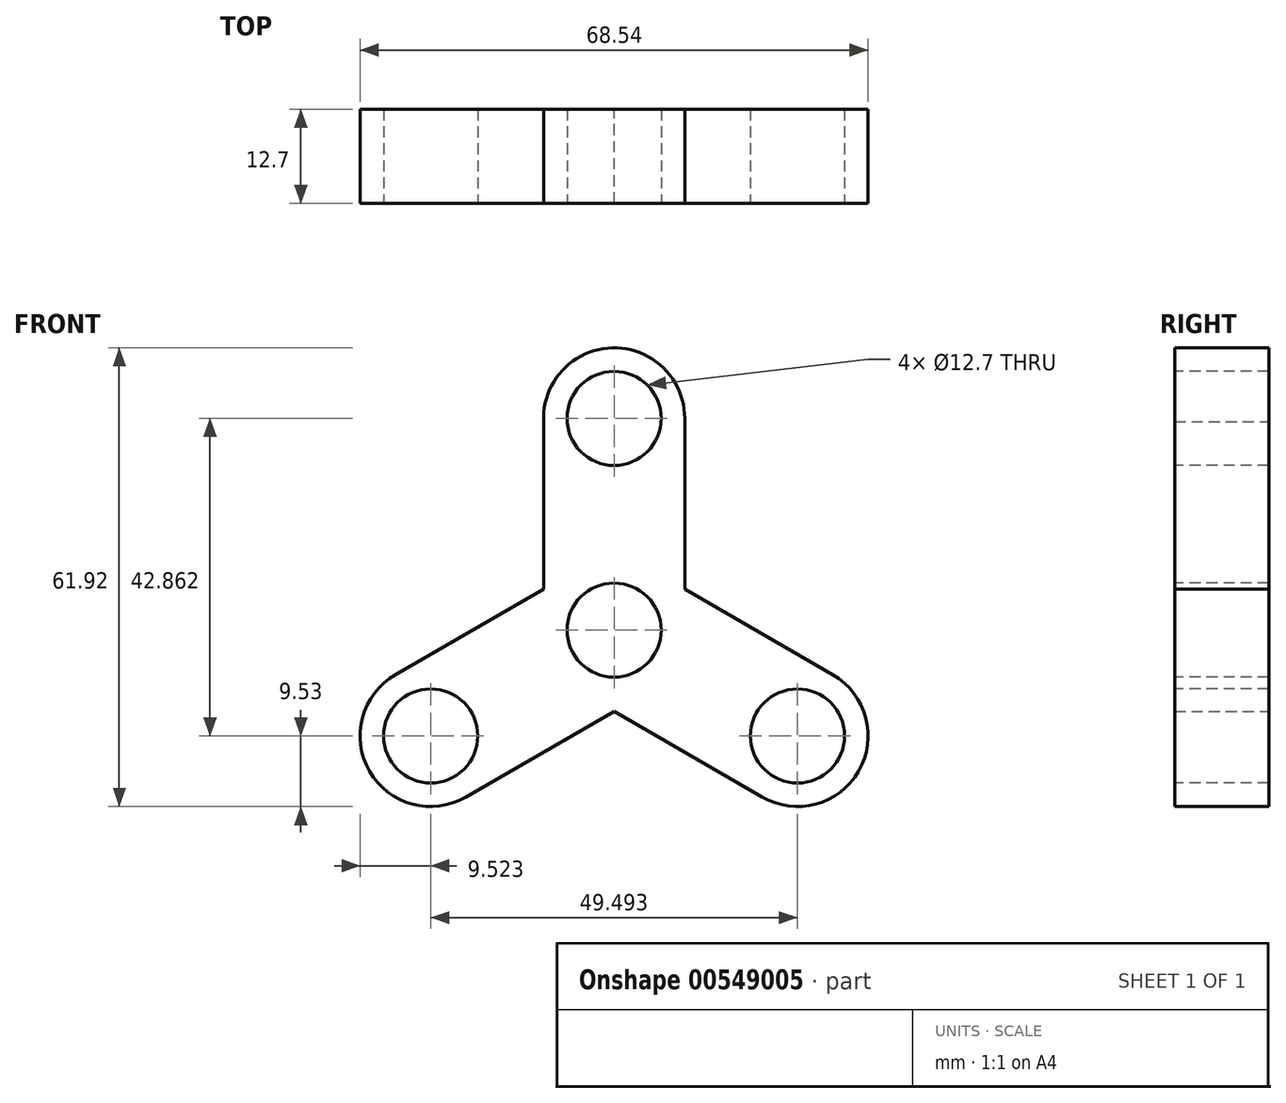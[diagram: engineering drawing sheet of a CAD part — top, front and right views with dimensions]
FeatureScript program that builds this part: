
annotation { "Feature Type Name" : "Feature", "Feature Type Description" : "" }
export const myFeature = defineFeature(function(context is Context, id is Id, definition is map)
    precondition{}
    {
        {
            var Q0;
            Q0=qCreatedBy(makeId("Front.planeOp"),FACE);
            var sketch = newSketch(context, id + "F0", { "sketchPlane" : qUnion([Q0])});
            skCircle(sketch, "E0", {"center": v(0, 42.86) * mm, "radius": 9.53 * mm});
            skCircle(sketch, "E1", {"center": v(-24.75, 0) * mm, "radius": 9.53 * mm});
            skCircle(sketch, "E2", {"center": v(24.75, 0) * mm, "radius": 9.53 * mm});
            skLineSegment(sketch, "E3", {"start": v(-29.5, 8.25) * mm, "end": v(-4.76, 22.54) * mm});
            skLineSegment(sketch, "E4", {"start": v(-19.98, -8.25) * mm, "end": v(4.76, 6.04) * mm});
            skLineSegment(sketch, "E5", {"start": v(9.52, 42.86) * mm, "end": v(9.53, 14.29) * mm});
            skLineSegment(sketch, "E6", {"start": v(-9.51, 42.4) * mm, "end": v(-9.51, 13.83) * mm});
            skLineSegment(sketch, "E7", {"start": v(29.5, 8.25) * mm, "end": v(4.76, 22.54) * mm});
            skLineSegment(sketch, "E8", {"start": v(19.98, -8.25) * mm, "end": v(-4.76, 6.04) * mm});
            skSolve(sketch);
        }
        {
            var Q0;
            {var subQ0=sQuery(id+"F0.wireOp",EDGE,"E0");var subQ1=makeQuery(id+"F0.imprint","INTERSECT",VERTEX,{"derivedFrom":[subQ0,sQuery(id+"F0.wireOp",EDGE,"E5")]});Q0=makeQuery(id+"F0.imprint","IMPRINT",FACE,{"disambiguationData":[TD([[makeQuery(id+"F0.imprint","IMPRINT",EDGE,{"disambiguationData":[TD([[subQ1,-1.0]])],"derivedFrom":subQ0}),1.0]])]});}
            var Q1;
            {var subQ12=sQuery(id+"F0.wireOp",EDGE,"E5");var subQ13=sQuery(id+"F0.wireOp",EDGE,"E0");var subQ14=makeQuery(id+"F0.imprint","INTERSECT",VERTEX,{"derivedFrom":[subQ13,subQ12]});Q1=makeQuery(id+"F0.imprint","IMPRINT",FACE,{"disambiguationData":[TD([[makeQuery(id+"F0.imprint","IMPRINT",EDGE,{"disambiguationData":[TD([[subQ14,1.0]])],"derivedFrom":subQ13}),-1.0]])]});}
            var Q2;
            {var subQ0=sQuery(id+"F0.wireOp",EDGE,"E1");var subQ1=makeQuery(id+"F0.imprint","INTERSECT",VERTEX,{"derivedFrom":[subQ0,sQuery(id+"F0.wireOp",EDGE,"E3")]});Q2=makeQuery(id+"F0.imprint","IMPRINT",FACE,{"disambiguationData":[TD([[makeQuery(id+"F0.imprint","IMPRINT",EDGE,{"disambiguationData":[TD([[subQ1,-1.0]])],"derivedFrom":subQ0}),1.0]])]});}
            var Q3;
            {var subQ0=sQuery(id+"F0.wireOp",EDGE,"E2");var subQ1=makeQuery(id+"F0.imprint","INTERSECT",VERTEX,{"derivedFrom":[subQ0,sQuery(id+"F0.wireOp",EDGE,"E7")]});Q3=makeQuery(id+"F0.imprint","IMPRINT",FACE,{"disambiguationData":[TD([[makeQuery(id+"F0.imprint","IMPRINT",EDGE,{"disambiguationData":[TD([[subQ1,-1.0]])],"derivedFrom":subQ0}),1.0]])]});}
            extrude(context, id + "F1", {"entities" : qUnion([Q0, Q1, Q2, Q3]), "depth" : 12.7 * mm, "offsetDistance" : 25.4 * mm});
        }
        {
            var Q0;
            Q0=makeQuery(id+"F1.opExtrude","CAP_FACE",FACE,{"disambiguationData":[OSD([sQuery(id+"F0.wireOp",EDGE,"E0"),sQuery(id+"F0.wireOp",EDGE,"E1"),sQuery(id+"F0.wireOp",EDGE,"E2"),sQuery(id+"F0.wireOp",EDGE,"E3"),sQuery(id+"F0.wireOp",EDGE,"E4"),sQuery(id+"F0.wireOp",EDGE,"E5"),sQuery(id+"F0.wireOp",EDGE,"E6"),sQuery(id+"F0.wireOp",EDGE,"E7"),sQuery(id+"F0.wireOp",EDGE,"E8")])],"isStart":false});
            var sketch = newSketch(context, id + "F2", { "sketchPlane" : qUnion([Q0])});
            skCircle(sketch, "E9", {"center": v(-24.75, 0) * mm, "radius": 6.35 * mm});
            skCircle(sketch, "E10", {"center": v(24.75, 0) * mm, "radius": 6.35 * mm});
            skCircle(sketch, "E11", {"center": v(0, 42.86) * mm, "radius": 6.35 * mm});
            skCircle(sketch, "E12", {"center": v(0, 14.29) * mm, "radius": 6.35 * mm});
            skSolve(sketch);
        }
        {
            var Q0;
            Q0=makeQuery(id+"F2.imprint","IMPRINT",FACE,{"disambiguationData":[TD([[makeQuery(id+"F2.imprint","IMPRINT",EDGE,{"derivedFrom":sQuery(id+"F2.wireOp",EDGE,"E9")}),1.0]])]});
            var Q1;
            Q1=makeQuery(id+"F2.imprint","IMPRINT",FACE,{"disambiguationData":[TD([[makeQuery(id+"F2.imprint","IMPRINT",EDGE,{"derivedFrom":sQuery(id+"F2.wireOp",EDGE,"E12")}),1.0]])]});
            var Q2;
            Q2=makeQuery(id+"F2.imprint","IMPRINT",FACE,{"disambiguationData":[TD([[makeQuery(id+"F2.imprint","IMPRINT",EDGE,{"derivedFrom":sQuery(id+"F2.wireOp",EDGE,"E11")}),1.0]])]});
            var Q3;
            Q3=makeQuery(id+"F2.imprint","IMPRINT",FACE,{"disambiguationData":[TD([[makeQuery(id+"F2.imprint","IMPRINT",EDGE,{"derivedFrom":sQuery(id+"F2.wireOp",EDGE,"E10")}),1.0]])]});
            extrude(context, id + "F3", {"entities" : qUnion([Q0, Q1, Q2, Q3]), "operationType" : NewBodyOperationType.REMOVE, "endBound" : BoundingType.THROUGH_ALL, "oppositeDirection" : true, "depth" : 25.4 * mm, "offsetDistance" : 25.4 * mm});
        }
    });
